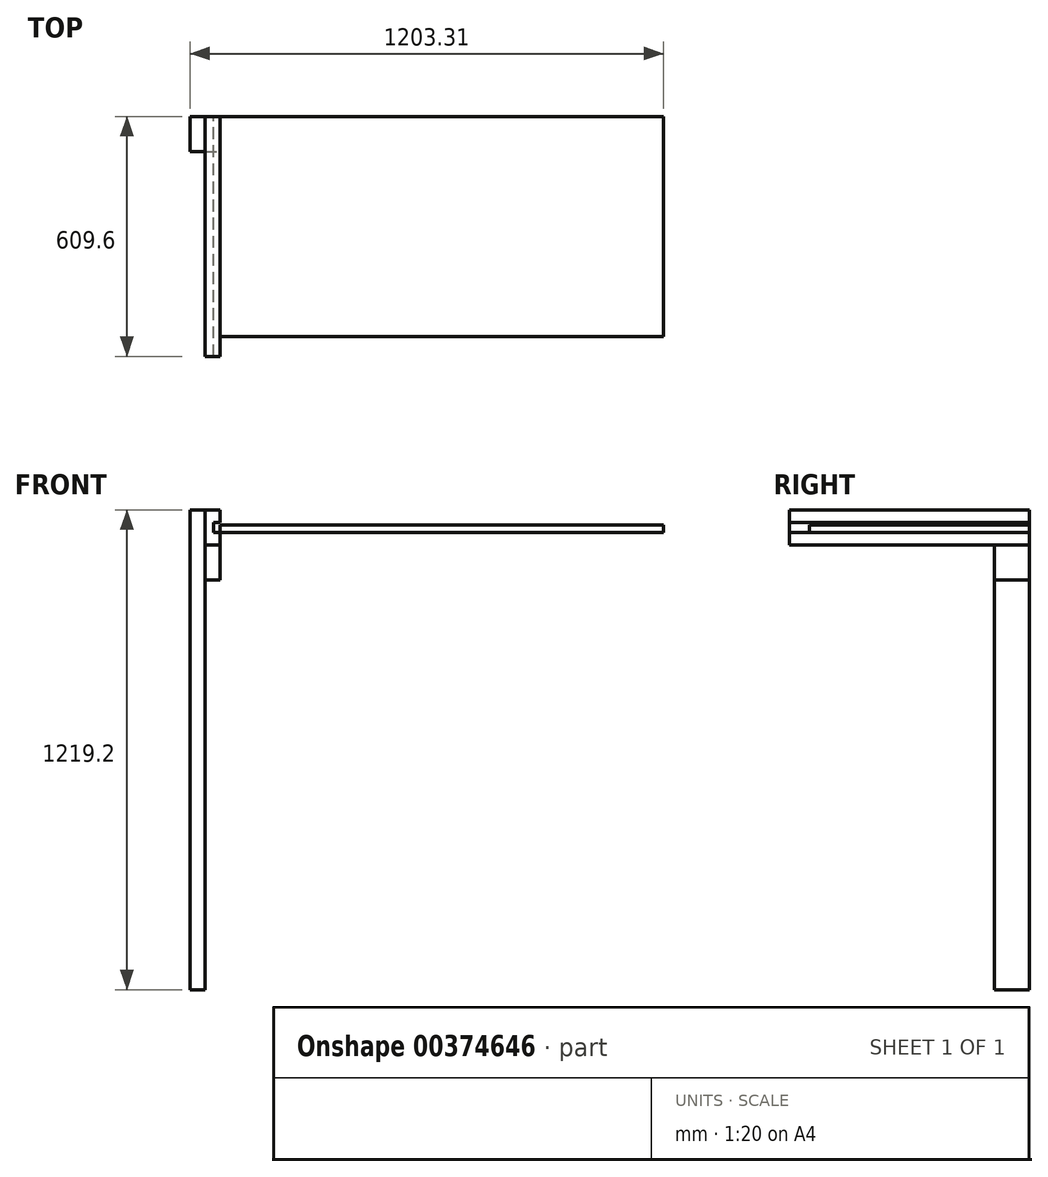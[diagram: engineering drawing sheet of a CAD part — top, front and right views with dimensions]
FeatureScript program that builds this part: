
annotation { "Feature Type Name" : "Feature", "Feature Type Description" : "" }
export const myFeature = defineFeature(function(context is Context, id is Id, definition is map)
    precondition{}
    {
        {
            var Q0;
            Q0=qCreatedBy(makeId("Front.planeOp"),FACE);
            var sketch = newSketch(context, id + "F0", { "sketchPlane" : qUnion([Q0])});
            skLineSegment(sketch, "E0.bottom", {"start": v(-98, 2367.14) * mm, "end": v(-59.9, 2367.14) * mm});
            skLineSegment(sketch, "E0.left", {"start": v(-98, 2367.14) * mm, "end": v(-98, 1147.94) * mm});
            skLineSegment(sketch, "E0.right", {"start": v(-59.9, 2367.14) * mm, "end": v(-59.9, 1147.94) * mm});
            skLineSegment(sketch, "E1.bottom", {"start": v(-59.9, 2367.14) * mm, "end": v(-21.8, 2367.14) * mm});
            skLineSegment(sketch, "E1.top", {"start": v(-59.9, 2278.24) * mm, "end": v(-21.8, 2278.24) * mm});
            skLineSegment(sketch, "E1.left", {"start": v(-59.9, 2367.14) * mm, "end": v(-59.9, 2278.24) * mm});
            skLineSegment(sketch, "E1.right", {"start": v(-21.8, 2367.14) * mm, "end": v(-21.8, 2278.24) * mm});
            skLineSegment(sketch, "E2.bottom", {"start": v(-21.8, 2309.99) * mm, "end": v(-37.7, 2309.99) * mm});
            skLineSegment(sketch, "E2.top", {"start": v(-21.8, 2335.39) * mm, "end": v(-37.7, 2335.39) * mm});
            skLineSegment(sketch, "E2.left", {"start": v(-21.8, 2322.69) * mm, "end": v(-21.8, 2348.09) * mm});
            skLineSegment(sketch, "E2.right", {"start": v(-37.7, 2309.99) * mm, "end": v(-37.7, 2335.39) * mm});
            skLineSegment(sketch, "E3.top", {"start": v(-59.9, 2189.34) * mm, "end": v(-21.8, 2189.34) * mm});
            skLineSegment(sketch, "E3.left", {"start": v(-59.9, 2278.24) * mm, "end": v(-59.9, 2189.34) * mm});
            skLineSegment(sketch, "E3.right", {"start": v(-21.8, 2278.24) * mm, "end": v(-21.8, 2189.34) * mm});
            skLineSegment(sketch, "E4.bottom", {"start": v(-37.7, 2309.99) * mm, "end": v(1105.3, 2309.99) * mm});
            skLineSegment(sketch, "E4.top", {"start": v(-37.7, 2328.4) * mm, "end": v(1105.3, 2328.4) * mm});
            skLineSegment(sketch, "E4.left", {"start": v(-37.7, 2309.99) * mm, "end": v(-37.7, 2328.4) * mm});
            skLineSegment(sketch, "E4.right", {"start": v(1105.3, 2309.99) * mm, "end": v(1105.3, 2328.4) * mm});
            skLineSegment(sketch, "E5", {"start": v(-98, 1147.94) * mm, "end": v(-59.9, 1147.94) * mm});
            skPoint(sketch, "E0.top.end.orphan", {"position": v(-59.9, -71.26) * mm});
            skPoint(sketch, "E0.top.start.orphan", {"position": v(-98, -71.26) * mm});
            skSolve(sketch);
        }
        {
            var Q0;
            {var subQ1=sQuery(id+"F0.wireOp",EDGE,"E1.bottom");Q0=makeQuery(id+"F0.imprint","IMPRINT",FACE,{"disambiguationData":[TD([[makeQuery(id+"F0.imprint","IMPRINT",EDGE,{"derivedFrom":subQ1}),-1.0]])]});}
            extrude(context, id + "F1", {"entities" : qUnion([Q0]), "depth" : 609.6 * mm});
        }
        {
            var Q0;
            Q0=makeQuery(id+"F0.imprint","IMPRINT",FACE,{"disambiguationData":[TD([[makeQuery(id+"F0.imprint","IMPRINT",EDGE,{"derivedFrom":sQuery(id+"F0.wireOp",EDGE,"E0.bottom")}),-1.0]])]});
            extrude(context, id + "F2", {"entities" : qUnion([Q0]), "depth" : 88.9 * mm});
        }
        {
            var Q0;
            Q0=makeQuery(id+"F0.imprint","IMPRINT",FACE,{"disambiguationData":[TD([[makeQuery(id+"F0.imprint","IMPRINT",EDGE,{"derivedFrom":sQuery(id+"F0.wireOp",EDGE,"E1.top")}),-1.0]])]});
            extrude(context, id + "F3", {"entities" : qUnion([Q0]), "depth" : 88.9 * mm});
        }
        {
            var Q0;
            {var subQ0=sQuery(id+"F0.wireOp",EDGE,"E4.right");Q0=makeQuery(id+"F0.imprint","IMPRINT",FACE,{"disambiguationData":[TD([[makeQuery(id+"F0.imprint","IMPRINT",EDGE,{"derivedFrom":subQ0}),1.0]])]});}
            var Q1;
            {var subQ0=sQuery(id+"F0.wireOp",EDGE,"E4.left");Q1=makeQuery(id+"F0.imprint","IMPRINT",FACE,{"disambiguationData":[TD([[makeQuery(id+"F0.imprint","IMPRINT",EDGE,{"derivedFrom":subQ0}),-1.0]])]});}
            extrude(context, id + "F4", {"entities" : qUnion([Q0, Q1]), "depth" : 558.8 * mm});
        }
    });
